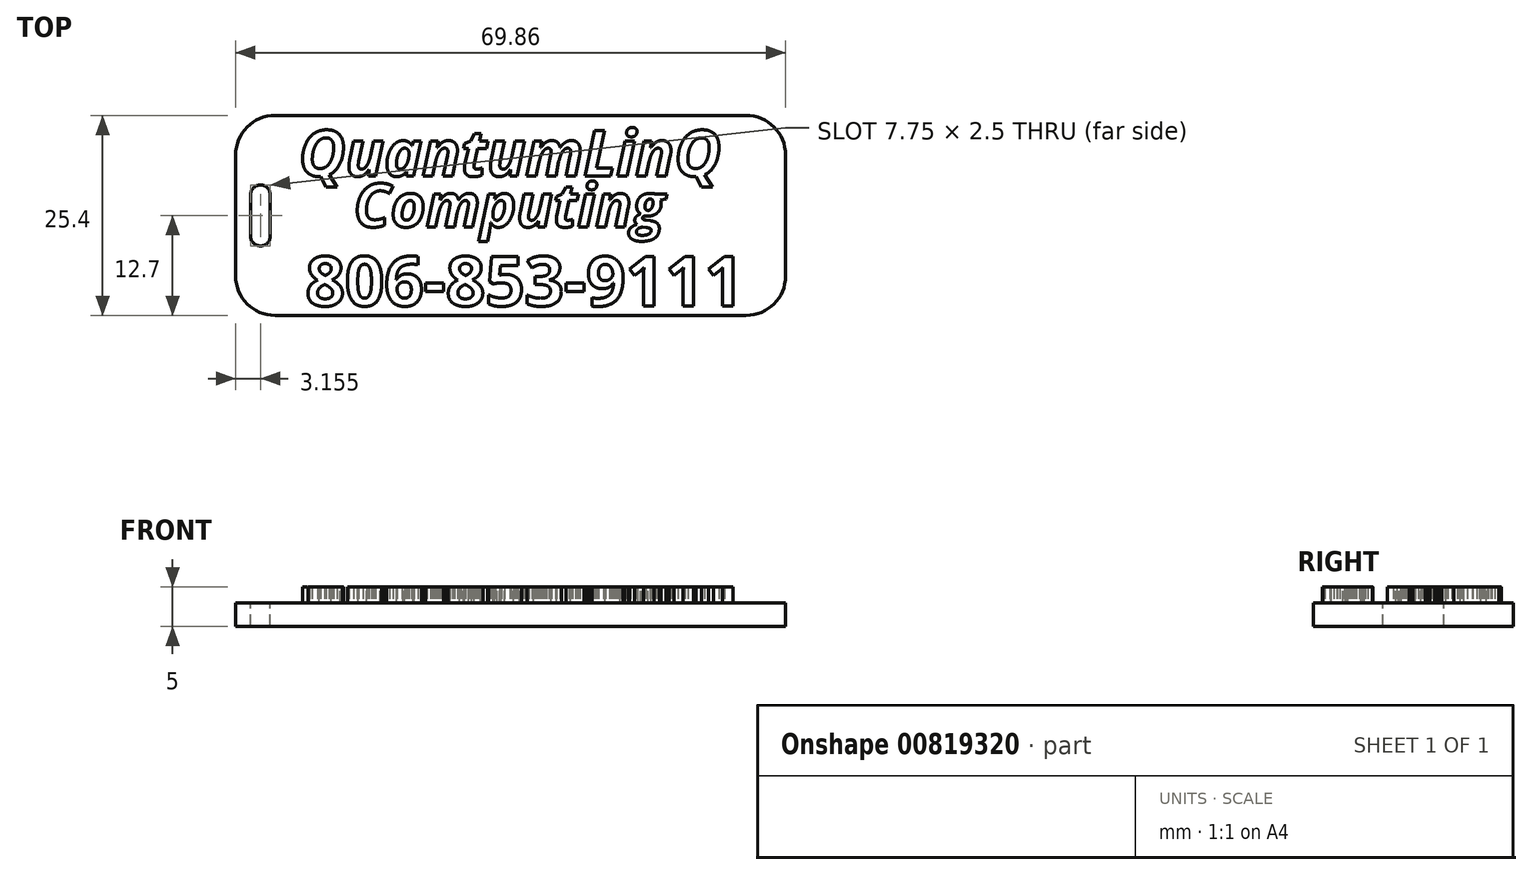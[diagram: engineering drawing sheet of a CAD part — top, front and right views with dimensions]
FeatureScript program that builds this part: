
annotation { "Feature Type Name" : "Feature", "Feature Type Description" : "" }
export const myFeature = defineFeature(function(context is Context, id is Id, definition is map)
    precondition{}
    {
        {
            var Q0;
            Q0=qCreatedBy(makeId("Top.planeOp"),FACE);
            var sketch = newSketch(context, id + "F0", { "sketchPlane" : qUnion([Q0])});
            skLineSegment(sketch, "E0.bottom", {"start": v(34.93, -12.7) * mm, "end": v(-34.93, -12.7) * mm});
            skLineSegment(sketch, "E0.top", {"start": v(34.93, 12.7) * mm, "end": v(-34.93, 12.7) * mm});
            skLineSegment(sketch, "E0.left", {"start": v(34.93, -12.7) * mm, "end": v(34.93, 12.7) * mm});
            skLineSegment(sketch, "E0.right", {"start": v(-34.93, -12.7) * mm, "end": v(-34.93, 12.7) * mm});
            skPoint(sketch, "E0.middle", {"position": v(0, 0) * mm});
            skSolve(sketch);
        }
        {
            var Q0;
            Q0=makeQuery(id+"F0.imprint","IMPRINT",FACE,{"disambiguationData":[TD([[makeQuery(id+"F0.imprint","IMPRINT",EDGE,{"derivedFrom":sQuery(id+"F0.wireOp",EDGE,"E0.bottom")}),-1.0]])]});
            extrude(context, id + "F1", {"entities" : qUnion([Q0]), "depth" : 3 * mm, "offsetDistance" : 25 * mm});
        }
        {
            var Q0;
            Q0=makeQuery(id+"F1.opExtrude","CAP_FACE",FACE,{"disambiguationData":[OSD([sQuery(id+"F0.wireOp",EDGE,"E0.bottom"),sQuery(id+"F0.wireOp",EDGE,"E0.top"),sQuery(id+"F0.wireOp",EDGE,"E0.left"),sQuery(id+"F0.wireOp",EDGE,"E0.right")])],"isStart":false});
            var sketch = newSketch(context, id + "F2", { "sketchPlane" : qUnion([Q0])});
            skText(sketch, "E1", { "text": "QuantumLinQ", "fontName": "OpenSans-BoldItalic.ttf"});
            skText(sketch, "E2", { "text": "Computing", "fontName": "OpenSans-BoldItalic.ttf"});
            skText(sketch, "E3", { "text": "806-853-9111", "fontName": "OpenSans-Bold.ttf"});
            const initialGuessF2  = {"E1": [-0.02691, 0.005, 1, 0, 0.00585], "E2": [-0.01994, -0.00145, 1, 0, 0.00552], "E3": [-0.02605, -0.01148, 1, 0, 0.00631]};
            skSetInitialGuess(sketch, initialGuessF2);
            skSolve(sketch);
        }
        {
            var Q0;
            Q0=makeQuery(id+"F1.opExtrude","SWEPT_EDGE",EDGE,{"disambiguationData":[OSD([sQuery(id+"F0.wireOp",EDGE,"E0.bottom"),sQuery(id+"F0.wireOp",EDGE,"E0.right")])]});
            var Q1;
            Q1=makeQuery(id+"F1.opExtrude","SWEPT_EDGE",EDGE,{"disambiguationData":[OSD([sQuery(id+"F0.wireOp",EDGE,"E0.top"),sQuery(id+"F0.wireOp",EDGE,"E0.right")])]});
            var Q2;
            Q2=makeQuery(id+"F1.opExtrude","SWEPT_EDGE",EDGE,{"disambiguationData":[OSD([sQuery(id+"F0.wireOp",EDGE,"E0.bottom"),sQuery(id+"F0.wireOp",EDGE,"E0.left")])]});
            var Q3;
            Q3=makeQuery(id+"F1.opExtrude","SWEPT_EDGE",EDGE,{"disambiguationData":[OSD([sQuery(id+"F0.wireOp",EDGE,"E0.top"),sQuery(id+"F0.wireOp",EDGE,"E0.left")])]});
            fillet(context, id + "F3", {"entities" : qUnion([Q0, Q1, Q2, Q3]), "radius" : 5 * mm, "tangentPropagation" : true, "allowEdgeOverflow" : false});
        }
        {
            var Q0;
            Q0=makeQuery(id+"F2.imprint","IMPRINT",FACE,{"disambiguationData":[TD([[makeQuery(id+"F2.imprint","IMPRINT",EDGE,{"derivedFrom":sQuery(id+"F2.wireOp",EDGE,"E1.sketch_text.stroke-0")}),-1.0]])]});
            var Q1;
            Q1=makeQuery(id+"F2.imprint","IMPRINT",FACE,{"disambiguationData":[TD([[makeQuery(id+"F2.imprint","IMPRINT",EDGE,{"derivedFrom":sQuery(id+"F2.wireOp",EDGE,"E1.sketch_text.stroke-23")}),-1.0]])]});
            var Q2;
            Q2=makeQuery(id+"F2.imprint","IMPRINT",FACE,{"disambiguationData":[TD([[makeQuery(id+"F2.imprint","IMPRINT",EDGE,{"derivedFrom":sQuery(id+"F2.wireOp",EDGE,"E1.sketch_text.stroke-40")}),-1.0]])]});
            var Q3;
            Q3=makeQuery(id+"F2.imprint","IMPRINT",FACE,{"disambiguationData":[TD([[makeQuery(id+"F2.imprint","IMPRINT",EDGE,{"derivedFrom":sQuery(id+"F2.wireOp",EDGE,"E1.sketch_text.stroke-65")}),-1.0]])]});
            var Q4;
            Q4=makeQuery(id+"F2.imprint","IMPRINT",FACE,{"disambiguationData":[TD([[makeQuery(id+"F2.imprint","IMPRINT",EDGE,{"derivedFrom":sQuery(id+"F2.wireOp",EDGE,"E1.sketch_text.stroke-82")}),-1.0]])]});
            var Q5;
            Q5=makeQuery(id+"F2.imprint","IMPRINT",FACE,{"disambiguationData":[TD([[makeQuery(id+"F2.imprint","IMPRINT",EDGE,{"derivedFrom":sQuery(id+"F2.wireOp",EDGE,"E1.sketch_text.stroke-101")}),-1.0]])]});
            var Q6;
            Q6=makeQuery(id+"F2.imprint","IMPRINT",FACE,{"disambiguationData":[TD([[makeQuery(id+"F2.imprint","IMPRINT",EDGE,{"derivedFrom":sQuery(id+"F2.wireOp",EDGE,"E1.sketch_text.stroke-118")}),-1.0]])]});
            var Q7;
            Q7=makeQuery(id+"F2.imprint","IMPRINT",FACE,{"disambiguationData":[TD([[makeQuery(id+"F2.imprint","IMPRINT",EDGE,{"derivedFrom":sQuery(id+"F2.wireOp",EDGE,"E1.sketch_text.stroke-146")}),-1.0]])]});
            var Q8;
            Q8=makeQuery(id+"F2.imprint","IMPRINT",FACE,{"disambiguationData":[TD([[makeQuery(id+"F2.imprint","IMPRINT",EDGE,{"derivedFrom":sQuery(id+"F2.wireOp",EDGE,"E1.sketch_text.stroke-159")}),-1.0]])]});
            var Q9;
            Q9=makeQuery(id+"F2.imprint","IMPRINT",FACE,{"disambiguationData":[TD([[makeQuery(id+"F2.imprint","IMPRINT",EDGE,{"derivedFrom":sQuery(id+"F2.wireOp",EDGE,"E1.sketch_text.stroke-152")}),-1.0]])]});
            var Q10;
            Q10=makeQuery(id+"F2.imprint","IMPRINT",FACE,{"disambiguationData":[TD([[makeQuery(id+"F2.imprint","IMPRINT",EDGE,{"derivedFrom":sQuery(id+"F2.wireOp",EDGE,"E1.sketch_text.stroke-163")}),-1.0]])]});
            var Q11;
            Q11=makeQuery(id+"F2.imprint","IMPRINT",FACE,{"disambiguationData":[TD([[makeQuery(id+"F2.imprint","IMPRINT",EDGE,{"derivedFrom":sQuery(id+"F2.wireOp",EDGE,"E1.sketch_text.stroke-180")}),-1.0]])]});
            var Q12;
            Q12=makeQuery(id+"F2.imprint","IMPRINT",FACE,{"disambiguationData":[TD([[makeQuery(id+"F2.imprint","IMPRINT",EDGE,{"derivedFrom":sQuery(id+"F2.wireOp",EDGE,"E2.sketch_text.stroke-0")}),-1.0]])]});
            var Q13;
            Q13=makeQuery(id+"F2.imprint","IMPRINT",FACE,{"disambiguationData":[TD([[makeQuery(id+"F2.imprint","IMPRINT",EDGE,{"derivedFrom":sQuery(id+"F2.wireOp",EDGE,"E2.sketch_text.stroke-18")}),-1.0]])]});
            var Q14;
            Q14=makeQuery(id+"F2.imprint","IMPRINT",FACE,{"disambiguationData":[TD([[makeQuery(id+"F2.imprint","IMPRINT",EDGE,{"derivedFrom":sQuery(id+"F2.wireOp",EDGE,"E2.sketch_text.stroke-36")}),-1.0]])]});
            var Q15;
            Q15=makeQuery(id+"F2.imprint","IMPRINT",FACE,{"disambiguationData":[TD([[makeQuery(id+"F2.imprint","IMPRINT",EDGE,{"derivedFrom":sQuery(id+"F2.wireOp",EDGE,"E2.sketch_text.stroke-64")}),-1.0]])]});
            var Q16;
            Q16=makeQuery(id+"F2.imprint","IMPRINT",FACE,{"disambiguationData":[TD([[makeQuery(id+"F2.imprint","IMPRINT",EDGE,{"derivedFrom":sQuery(id+"F2.wireOp",EDGE,"E2.sketch_text.stroke-89")}),-1.0]])]});
            var Q17;
            Q17=makeQuery(id+"F2.imprint","IMPRINT",FACE,{"disambiguationData":[TD([[makeQuery(id+"F2.imprint","IMPRINT",EDGE,{"derivedFrom":sQuery(id+"F2.wireOp",EDGE,"E2.sketch_text.stroke-106")}),-1.0]])]});
            var Q18;
            Q18=makeQuery(id+"F2.imprint","IMPRINT",FACE,{"disambiguationData":[TD([[makeQuery(id+"F2.imprint","IMPRINT",EDGE,{"derivedFrom":sQuery(id+"F2.wireOp",EDGE,"E2.sketch_text.stroke-132")}),-1.0]])]});
            var Q19;
            Q19=makeQuery(id+"F2.imprint","IMPRINT",FACE,{"disambiguationData":[TD([[makeQuery(id+"F2.imprint","IMPRINT",EDGE,{"derivedFrom":sQuery(id+"F2.wireOp",EDGE,"E2.sketch_text.stroke-125")}),-1.0]])]});
            var Q20;
            Q20=makeQuery(id+"F2.imprint","IMPRINT",FACE,{"disambiguationData":[TD([[makeQuery(id+"F2.imprint","IMPRINT",EDGE,{"derivedFrom":sQuery(id+"F2.wireOp",EDGE,"E2.sketch_text.stroke-136")}),-1.0]])]});
            var Q21;
            Q21=makeQuery(id+"F2.imprint","IMPRINT",FACE,{"disambiguationData":[TD([[makeQuery(id+"F2.imprint","IMPRINT",EDGE,{"derivedFrom":sQuery(id+"F2.wireOp",EDGE,"E2.sketch_text.stroke-153")}),-1.0]])]});
            var Q22;
            Q22=makeQuery(id+"F2.imprint","IMPRINT",FACE,{"disambiguationData":[TD([[makeQuery(id+"F2.imprint","IMPRINT",EDGE,{"derivedFrom":sQuery(id+"F2.wireOp",EDGE,"E3.sketch_text.stroke-0")}),-1.0]])]});
            var Q23;
            Q23=makeQuery(id+"F2.imprint","IMPRINT",FACE,{"disambiguationData":[TD([[makeQuery(id+"F2.imprint","IMPRINT",EDGE,{"derivedFrom":sQuery(id+"F2.wireOp",EDGE,"E3.sketch_text.stroke-31")}),-1.0]])]});
            var Q24;
            Q24=makeQuery(id+"F2.imprint","IMPRINT",FACE,{"disambiguationData":[TD([[makeQuery(id+"F2.imprint","IMPRINT",EDGE,{"derivedFrom":sQuery(id+"F2.wireOp",EDGE,"E3.sketch_text.stroke-47")}),-1.0]])]});
            var Q25;
            Q25=makeQuery(id+"F2.imprint","IMPRINT",FACE,{"disambiguationData":[TD([[makeQuery(id+"F2.imprint","IMPRINT",EDGE,{"derivedFrom":sQuery(id+"F2.wireOp",EDGE,"E3.sketch_text.stroke-72")}),-1.0]])]});
            var Q26;
            Q26=makeQuery(id+"F2.imprint","IMPRINT",FACE,{"disambiguationData":[TD([[makeQuery(id+"F2.imprint","IMPRINT",EDGE,{"derivedFrom":sQuery(id+"F2.wireOp",EDGE,"E3.sketch_text.stroke-76")}),-1.0]])]});
            var Q27;
            Q27=makeQuery(id+"F2.imprint","IMPRINT",FACE,{"disambiguationData":[TD([[makeQuery(id+"F2.imprint","IMPRINT",EDGE,{"derivedFrom":sQuery(id+"F2.wireOp",EDGE,"E3.sketch_text.stroke-107")}),-1.0]])]});
            var Q28;
            Q28=makeQuery(id+"F2.imprint","IMPRINT",FACE,{"disambiguationData":[TD([[makeQuery(id+"F2.imprint","IMPRINT",EDGE,{"derivedFrom":sQuery(id+"F2.wireOp",EDGE,"E3.sketch_text.stroke-127")}),-1.0]])]});
            var Q29;
            Q29=makeQuery(id+"F2.imprint","IMPRINT",FACE,{"disambiguationData":[TD([[makeQuery(id+"F2.imprint","IMPRINT",EDGE,{"derivedFrom":sQuery(id+"F2.wireOp",EDGE,"E3.sketch_text.stroke-154")}),-1.0]])]});
            var Q30;
            Q30=makeQuery(id+"F2.imprint","IMPRINT",FACE,{"disambiguationData":[TD([[makeQuery(id+"F2.imprint","IMPRINT",EDGE,{"derivedFrom":sQuery(id+"F2.wireOp",EDGE,"E3.sketch_text.stroke-158")}),-1.0]])]});
            var Q31;
            Q31=makeQuery(id+"F2.imprint","IMPRINT",FACE,{"disambiguationData":[TD([[makeQuery(id+"F2.imprint","IMPRINT",EDGE,{"derivedFrom":sQuery(id+"F2.wireOp",EDGE,"E3.sketch_text.stroke-184")}),-1.0]])]});
            var Q32;
            Q32=makeQuery(id+"F2.imprint","IMPRINT",FACE,{"disambiguationData":[TD([[makeQuery(id+"F2.imprint","IMPRINT",EDGE,{"derivedFrom":sQuery(id+"F2.wireOp",EDGE,"E3.sketch_text.stroke-194")}),-1.0]])]});
            var Q33;
            Q33=makeQuery(id+"F2.imprint","IMPRINT",FACE,{"disambiguationData":[TD([[makeQuery(id+"F2.imprint","IMPRINT",EDGE,{"derivedFrom":sQuery(id+"F2.wireOp",EDGE,"E3.sketch_text.stroke-204")}),-1.0]])]});
            extrude(context, id + "F4", {"entities" : qUnion([Q0, Q1, Q2, Q3, Q4, Q5, Q6, Q7, Q8, Q9, Q10, Q11, Q12, Q13, Q14, Q15, Q16, Q17, Q18, Q19, Q20, Q21, Q22, Q23, Q24, Q25, Q26, Q27, Q28, Q29, Q30, Q31, Q32, Q33]), "operationType" : NewBodyOperationType.ADD, "depth" : 2 * mm, "offsetDistance" : 25 * mm});
        }
        {
            var Q0;
            {var subQ0=sQuery(id+"F0.wireOp",EDGE,"E0.right");var subQ1=sQuery(id+"F0.wireOp",EDGE,"E0.top");var subQ2=sQuery(id+"F0.wireOp",EDGE,"E0.left");var subQ3=sQuery(id+"F0.wireOp",EDGE,"E0.bottom");Q0=makeQuery(id+"F4.boolean.opBoolean","SPLIT",FACE,{"disambiguationData":[TD([makeQuery(id+"F1.opExtrude","SWEPT_FACE",FACE,{"disambiguationData":[OSD([subQ3])]})])],"derivedFrom":makeQuery(id+"F1.opExtrude","CAP_FACE",FACE,{"disambiguationData":[OSD([subQ3,subQ1,subQ2,subQ0])],"isStart":false})});}
            var sketch = newSketch(context, id + "F5", { "sketchPlane" : qUnion([Q0])});
            skLineSegment(sketch, "E4.left", {"start": v(-30.52, -2.62) * mm, "end": v(-30.52, 2.62) * mm});
            skLineSegment(sketch, "E4.right", {"start": v(-33.02, -2.63) * mm, "end": v(-33.02, 2.62) * mm});
            skPoint(sketch, "E4.middle", {"position": v(-31.77, 0) * mm});
            skArc(sketch, "E5", {"start": v(-33.02, 2.62) * mm, "mid": v(-31.77, 3.88) * mm, "end": v(-30.52, 2.62) * mm});
            skArc(sketch, "E6", {"start": v(-33.02, -2.63) * mm, "mid": v(-31.77, -3.88) * mm, "end": v(-30.52, -2.63) * mm});
            skSolve(sketch);
        }
        {
            var Q0;
            Q0=makeQuery(id+"F5.imprint","IMPRINT",FACE,{"disambiguationData":[TD([[makeQuery(id+"F5.imprint","IMPRINT",EDGE,{"derivedFrom":sQuery(id+"F5.wireOp",EDGE,"E4.left")}),1.0]])]});
            extrude(context, id + "F6", {"entities" : qUnion([Q0]), "operationType" : NewBodyOperationType.REMOVE, "oppositeDirection" : true, "depth" : 25 * mm, "offsetDistance" : 25 * mm});
        }
    });
